# Revit family: Haworth_Compose_Worksurface_TransitionRectangular
name_source: partatom
category: Furniture Systems
revit_build: Autodesk Revit 2018 (Build: 20170223_1515(x64)
units: mm (PartAtom-declared; Revit-internal decimal feet)

## family parameters
Always vertical = Yes
Cut with Voids When Loaded = No
OmniClass Number = 23.40.70.14.64.21
OmniClass Title = Systems Furniture
Part Type = Normal
Room Calculation Point = No
Round Connector Dimension = Use Diameter
Shared = No
Work Plane-Based = No

## types (14) — shared parameters
Actual Height = 29"
Assembly Code = E2020200
Cantilever Bracket = Yes
Cantilever Bracket Location = 1 3/4"
Custom Size = No
Description = Haworth - Worksurface - Compose Transition - Rectangular
End Support Location = 1 3/4"
Height = 29"
Manufacturer = Haworth
Max. Height = 32"
Max. Width = 60"
Min. Height = 26"
Min. Width = 24"
Min/Max Height = 26-32 in.
Min/Max Width = 24-60 in. @ 6 in. increments
Model = WURT
Revision Number = 4
Size = Verify Final Dim. w/ Haworth
Standard Depths = 18/24 in., 24/30 in.
Support Column = No
Support Finish = Haworth _ Paint _ Metallic Champagne
Support Height = 27 13/16"
Support Location_Front_Back = 3"
Support Location_Side = 1 3/4"
Support P Leg = No
Support Panel = No
Support Post_45 Degree = No
Support Post_90 Degree = No
Sustainability Info = https://www.haworth.com
Top Thickness = 1 3/16"
Transition Depth = 6"
URL = www.haworth.com
URL - Product = http://www.haworth.com
Warranty = http://www.haworth.com
Worksurface Edge Finish = Haworth _ Laminate _ Maple H-AE
Worksurface Finish = Haworth _ Laminate _ Maple H-AE

## per-type parameters (varying)
| type | 18in_24in Worksurface | 24in_30in Worksurface | Actual Width | Long Side Depth | Radius 1 | Radius 2 | Radius 2 Center | Short Side Depth | Width |
| 24w 18/24d | Yes | No | 24" | 24" | 12" | 30" | 23 15/16" | 18" | 24" |
| 30w 18/24d | Yes | No | 30" | 24" | 12" | 30" | 23 15/16" | 18" | 30" |
| 36w 18/24d | Yes | No | 36" | 24" | 12" | 30" | 23 15/16" | 18" | 36" |
| 42w 18/24d | Yes | No | 42" | 24" | 19" | 48" | 41 123/128" | 18" | 42" |
| 48w 18/24d | Yes | No | 48" | 24" | 19" | 48" | 41 123/128" | 18" | 48" |
| 54w 18/24d | Yes | No | 54" | 24" | 19" | 48" | 41 123/128" | 18" | 54" |
| 60w 18/24d | Yes | No | 60" | 24" | 19" | 48" | 41 123/128" | 18" | 60" |
| 24w 24/30d | No | Yes | 24" | 30" | 12" | 30" | 23 15/16" | 24" | 24" |
| 30w 24/30d | No | Yes | 30" | 30" | 12" | 30" | 23 15/16" | 24" | 30" |
| 36w 24/30d | No | Yes | 36" | 30" | 12" | 30" | 23 15/16" | 24" | 36" |
| 42w 24/30d | No | Yes | 42" | 30" | 19" | 48" | 41 123/128" | 24" | 42" |
| 48w 24/30d | No | Yes | 48" | 30" | 19" | 48" | 41 123/128" | 24" | 48" |
| 54w 24/30d | No | Yes | 54" | 30" | 19" | 48" | 41 123/128" | 24" | 54" |
| 60w 24/30d | No | Yes | 60" | 30" | 19" | 48" | 41 123/128" | 24" | 60" |

## geometry (parser evidence)
native form markers: Blend x4, Sweep x8
no freeform markers — native parametric forms only
